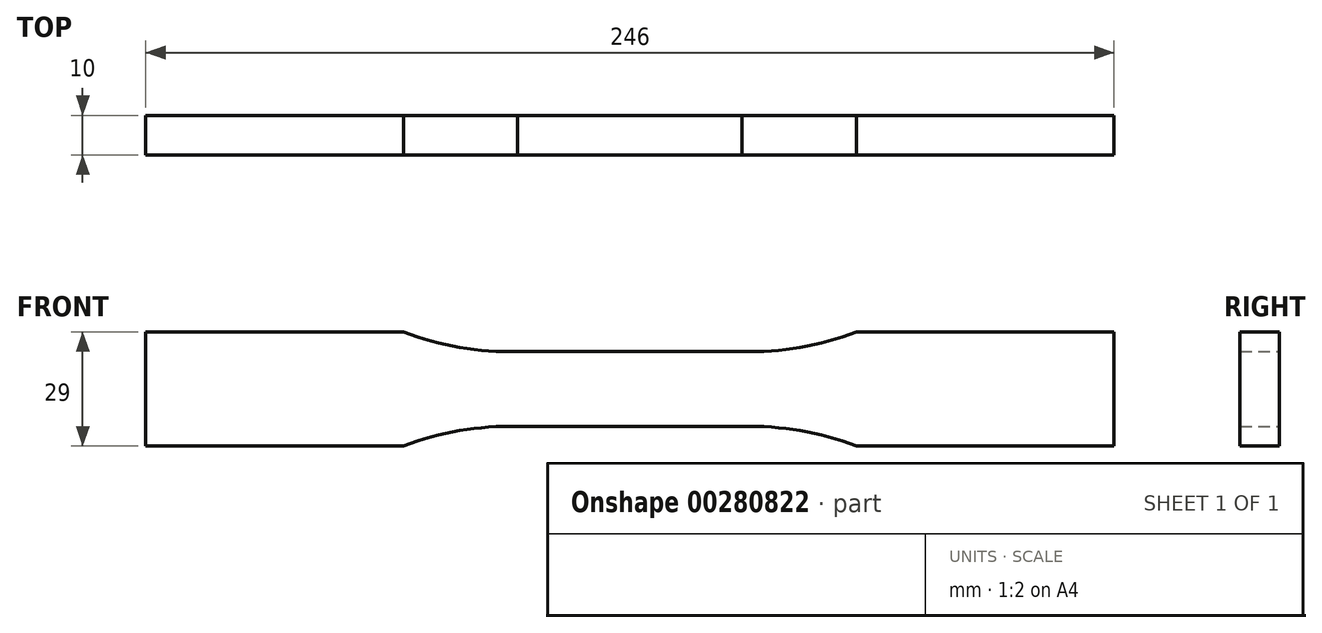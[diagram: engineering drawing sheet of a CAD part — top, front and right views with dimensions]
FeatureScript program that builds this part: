
annotation { "Feature Type Name" : "Feature", "Feature Type Description" : "" }
export const myFeature = defineFeature(function(context is Context, id is Id, definition is map)
    precondition{}
    {
        {
            var Q0;
            Q0=qCreatedBy(makeId("Front.planeOp"),FACE);
            var sketch = newSketch(context, id + "F0", { "sketchPlane" : qUnion([Q0])});
            skLineSegment(sketch, "E0", {"start": v(0, 9.5) * mm, "end": v(28.5, 9.5) * mm});
            skArc(sketch, "E1", {"start": v(28.5, 9.5) * mm, "mid": v(43.24, 10.58) * mm, "end": v(57.5, 14.5) * mm});
            skLineSegment(sketch, "E2", {"start": v(57.5, 14.5) * mm, "end": v(123, 14.5) * mm});
            skLineSegment(sketch, "E3.MirrorCS", {"start": v(57.5, -14.5) * mm, "end": v(123, -14.5) * mm});
            skLineSegment(sketch, "E4.MirrorCS", {"start": v(0, -9.5) * mm, "end": v(28.5, -9.5) * mm});
            skArc(sketch, "E5.MirrorCS", {"start": v(28.5, -9.5) * mm, "mid": v(43.24, -10.58) * mm, "end": v(57.5, -14.5) * mm});
            skLineSegment(sketch, "E6.MirrorCS", {"start": v(0, -9.5) * mm, "end": v(-28.5, -9.5) * mm});
            skArc(sketch, "E7.MirrorCS", {"start": v(-28.5, 9.5) * mm, "mid": v(-43.24, 10.58) * mm, "end": v(-57.5, 14.5) * mm});
            skLineSegment(sketch, "E8.MirrorCS", {"start": v(-57.5, 14.5) * mm, "end": v(-123, 14.5) * mm});
            skLineSegment(sketch, "E9.MirrorCS", {"start": v(-57.5, -14.5) * mm, "end": v(-123, -14.5) * mm});
            skLineSegment(sketch, "E10.MirrorCS", {"start": v(0, 9.5) * mm, "end": v(-28.5, 9.5) * mm});
            skArc(sketch, "E11.MirrorCS", {"start": v(-28.5, -9.5) * mm, "mid": v(-43.24, -10.58) * mm, "end": v(-57.5, -14.5) * mm});
            skLineSegment(sketch, "E12", {"start": v(123, 14.5) * mm, "end": v(123, -14.5) * mm});
            skLineSegment(sketch, "E13", {"start": v(-123, 14.5) * mm, "end": v(-123, -14.5) * mm});
            skSolve(sketch);
        }
        {
            var Q0;
            Q0=makeQuery(id+"F0.imprint","IMPRINT",FACE,{"disambiguationData":[TD([[makeQuery(id+"F0.imprint","IMPRINT",EDGE,{"derivedFrom":sQuery(id+"F0.wireOp",EDGE,"E4.MirrorCS")}),1.0]])]});
            extrude(context, id + "F1", {"entities" : qUnion([Q0]), "endBound" : BoundingType.SYMMETRIC, "depth" : 10 * mm});
        }
    });
